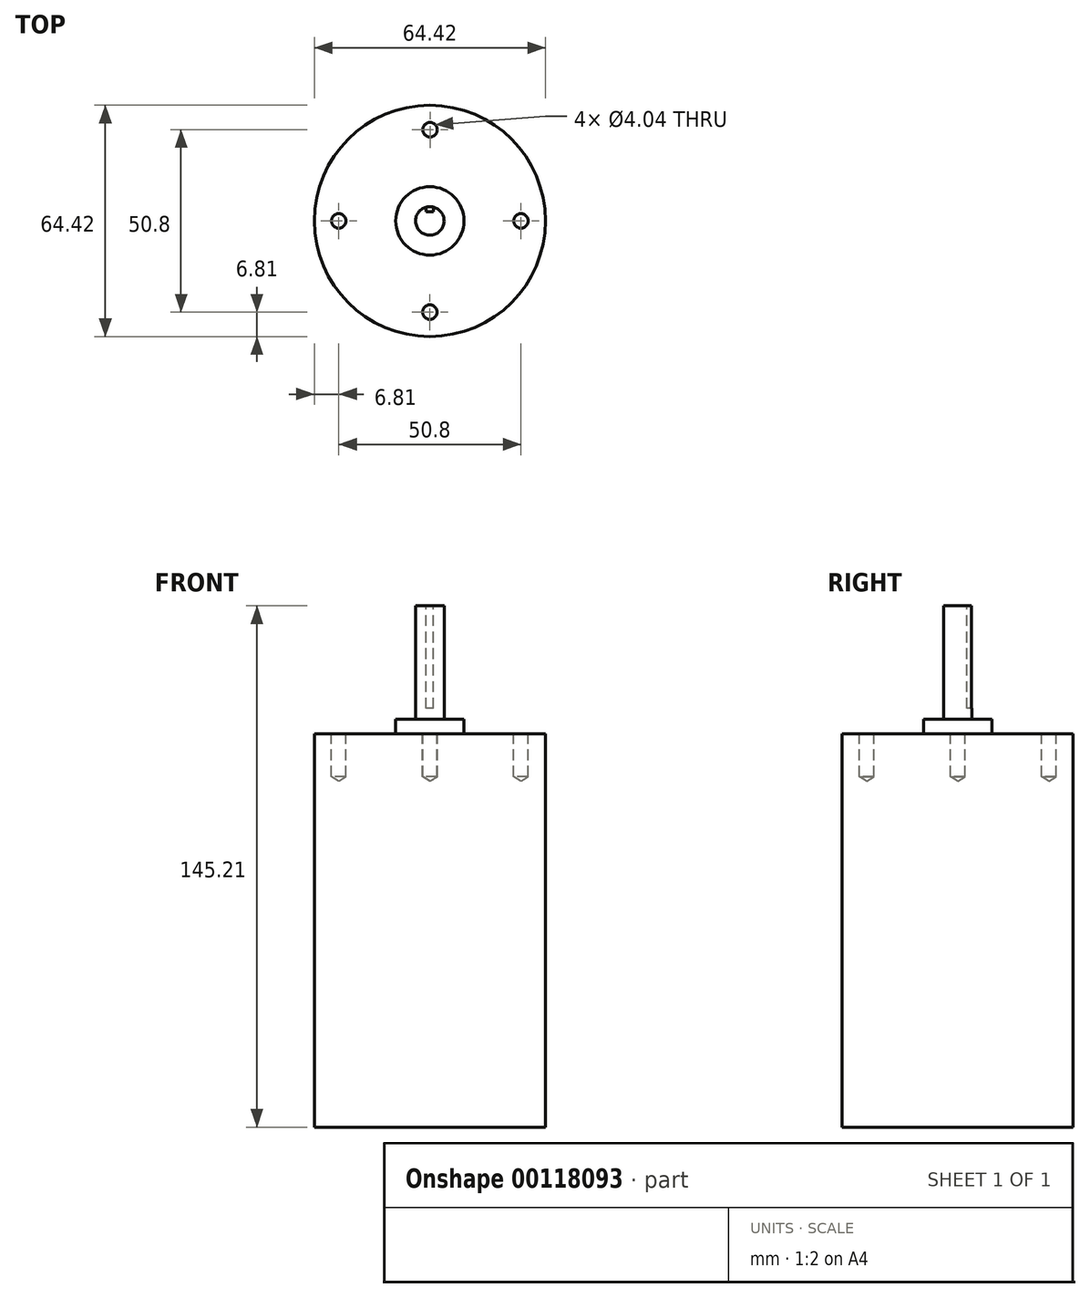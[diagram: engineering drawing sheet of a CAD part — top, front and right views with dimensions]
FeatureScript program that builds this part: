
annotation { "Feature Type Name" : "Feature", "Feature Type Description" : "" }
export const myFeature = defineFeature(function(context is Context, id is Id, definition is map)
    precondition{}
    {
        {
            var Q0;
            Q0=qCreatedBy(makeId("Top.planeOp"),FACE);
            var sketch = newSketch(context, id + "F0", { "sketchPlane" : qUnion([Q0])});
            skCircle(sketch, "E0", {"center": v(0, 0) * mm, "radius": 32.2 * mm});
            skSolve(sketch);
        }
        {
            var Q0;
            Q0=makeQuery(id+"F0.imprint","IMPRINT",FACE,{"disambiguationData":[TD([[makeQuery(id+"F0.imprint","IMPRINT",EDGE,{"derivedFrom":sQuery(id+"F0.wireOp",EDGE,"E0")}),1.0]])]});
            extrude(context, id + "F1", {"entities" : qUnion([Q0]), "depth" : 109.6 * mm});
        }
        {
            var Q0;
            Q0=makeQuery(id+"F1.opExtrude","CAP_FACE",FACE,{"disambiguationData":[OSD([sQuery(id+"F0.wireOp",EDGE,"E0")])],"isStart":false});
            var sketch = newSketch(context, id + "F2", { "sketchPlane" : qUnion([Q0])});
            skCircle(sketch, "E1", {"center": v(0, 0) * mm, "radius": 9.53 * mm});
            skSolve(sketch);
        }
        {
            var Q0;
            Q0=makeQuery(id+"F2.imprint","IMPRINT",FACE,{"disambiguationData":[TD([[makeQuery(id+"F2.imprint","IMPRINT",EDGE,{"derivedFrom":sQuery(id+"F2.wireOp",EDGE,"E1")}),1.0]])]});
            extrude(context, id + "F3", {"entities" : qUnion([Q0]), "operationType" : NewBodyOperationType.ADD, "depth" : 4 * mm});
        }
        {
            var Q0;
            Q0=makeQuery(id+"F3.opExtrude","CAP_FACE",FACE,{"disambiguationData":[OSD([sQuery(id+"F2.wireOp",EDGE,"E1")])],"isStart":false});
            var sketch = newSketch(context, id + "F4", { "sketchPlane" : qUnion([Q0])});
            skCircle(sketch, "E2", {"center": v(0, 0) * mm, "radius": 3.98 * mm});
            skSolve(sketch);
        }
        {
            var Q0;
            Q0=makeQuery(id+"F4.imprint","IMPRINT",FACE,{"disambiguationData":[TD([[makeQuery(id+"F4.imprint","IMPRINT",EDGE,{"derivedFrom":sQuery(id+"F4.wireOp",EDGE,"E2")}),1.0]])]});
            extrude(context, id + "F5", {"entities" : qUnion([Q0]), "operationType" : NewBodyOperationType.ADD, "depth" : (35.6 - 4) * mm});
        }
        {
            var Q0;
            Q0=makeQuery(id+"F5.opExtrude","CAP_FACE",FACE,{"disambiguationData":[OSD([sQuery(id+"F4.wireOp",EDGE,"E2")])],"isStart":false});
            var sketch = newSketch(context, id + "F6", { "sketchPlane" : qUnion([Q0])});
            skLineSegment(sketch, "E3.bottom", {"start": v(0.95, 4.89) * mm, "end": v(-1.05, 4.89) * mm});
            skLineSegment(sketch, "E3.top", {"start": v(0.95, 2.5) * mm, "end": v(-1.05, 2.5) * mm});
            skLineSegment(sketch, "E3.left", {"start": v(0.95, 4.89) * mm, "end": v(0.95, 2.5) * mm});
            skLineSegment(sketch, "E3.right", {"start": v(-1.05, 4.89) * mm, "end": v(-1.05, 2.5) * mm});
            skLineSegment(sketch, "E4", {"start": v(0, 0) * mm, "end": v(0, 2.5) * mm, "construction": true});
            skSolve(sketch);
        }
        {
            var Q0;
            {var subQ0=sQuery(id+"F6.wireOp",EDGE,"E3.top");Q0=makeQuery(id+"F6.imprint","IMPRINT",FACE,{"disambiguationData":[TD([[makeQuery(id+"F6.imprint","IMPRINT",EDGE,{"derivedFrom":subQ0}),-1.0]])]});}
            extrude(context, id + "F7", {"entities" : qUnion([Q0]), "operationType" : NewBodyOperationType.REMOVE, "oppositeDirection" : true, "depth" : 28.6 * mm});
        }
        {
            var Q0;
            Q0=makeQuery(id+"F1.opExtrude","CAP_FACE",FACE,{"disambiguationData":[OSD([sQuery(id+"F0.wireOp",EDGE,"E0")])],"isStart":false});
            var sketch = newSketch(context, id + "F8", { "sketchPlane" : qUnion([Q0])});
            skCircle(sketch, "E5", {"center": v(0, 0) * mm, "radius": 25.4 * mm, "construction": true});
            skLineSegment(sketch, "E6", {"start": v(0, 0) * mm, "end": v(-25.4, 0) * mm, "construction": true});
            skLineSegment(sketch, "E7", {"start": v(0, 0) * mm, "end": v(0.05, 25.4) * mm, "construction": true});
            skLineSegment(sketch, "E8", {"start": v(0, 0) * mm, "end": v(25.4, 0) * mm, "construction": true});
            skLineSegment(sketch, "E9", {"start": v(0, 0) * mm, "end": v(0, -25.4) * mm, "construction": true});
            skSolve(sketch);
        }
        {
            var Q0;
            Q0=sQuery(id+"F8.wireOp",VERTEX,"E7.end");
            var Q1;
            Q1=sQuery(id+"F8.wireOp",VERTEX,"E8.end");
            var Q2;
            Q2=sQuery(id+"F8.wireOp",VERTEX,"E6.end");
            var Q3;
            Q3=sQuery(id+"F8.wireOp",VERTEX,"E9.end");
            var Q4;
            Q4=makeQuery(id+"F1.opExtrude","SWEPT_BODY",BODY,{"disambiguationData":[OSD([sQuery(id+"F0.wireOp",EDGE,"E0")])]});
            hole(context, id + "F9", {"style" : HoleStyle.SIMPLE, "endStyle" : HoleEndStyle.BLIND, "standardTappedOrClearance" : lookupTablePath({ "standard" : "ANSI", "engagement" : "75%", "pitch" : "32 tpi", "size" : "#10", "type" : "Tapped" }), "standardBlindInLast" : lookupTablePath({ "standard" : "ANSI", "engagement" : "75%", "pitch" : "32 tpi", "size" : "#10", "type" : "Tapped" }), "holeDiameter" : 4.04 * mm, "holeDepth" : 12 * mm, "startFromSketch" : true, "locations" : qUnion([Q0, Q1, Q2, Q3]), "scope" : qUnion([Q4]), "majorDiameter" : 4.83 * mm});
        }
    });
